# Revit family: Gira_277603
name_source: partatom
category: Electrical Fixtures
revit_build: Autodesk Revit 2017 (Build: 20160225_1515(x64)
units: mm (PartAtom-declared; Revit-internal decimal feet)

## family parameters
Cut with Voids When Loaded = No
Host = Face
Maintain Annotation Orientation = Yes
Part Type = Normal
Room Calculation Point = No
Round Connector Dimension = Use Diameter
Shared = No

## types (1)
- Sock.BS 13 A SH System 55 p.white
    Antibacterial treatment = No
    Available = No
    BIM (1) = https://media.stage.bim.site
    Category = Socket outlet
    Colour = White
    Connection type = Screwed terminal
    Cremeweiß glänzend = Cremeweiß glänzend
    Data sheet (1) = https://katalog.gira.de
    Default Elevation = 1219 mm
    Description = Sock.BS13A SH Sys55 PW,Socket outlet British Standard (BS 1363-2) 13 A 250 V~ with shutter,System 55, Support ring 71 x 71 mm,pure white glossy,Features:,- With screw terminals.,- For screw mounting only.
    Eject-mechanism = No
    Fault current protection = No
    Für "erschwerte Bedingungen" (nach VDE) (*de-DE) = No
    GTIN = 4010337079354
    HAN = 277603
    Halogen free = Yes
    HeinzeBIM = https://bimportal.heinze.de
    Imprint/indication = Without imprint
    Insulated mounting = No
    Label space/information surface = No
    Lockable = No
    Manufacturer = Gira
    Manufacturer URL = https://www.gira.de
    Material = Plastic
    Material quality = Thermoplastic
    Model = British Standard
    Mounting method = Flush mounted (plaster)
    Name = Sock.BS 13 A SH System 55 p.white
    Nominal current = 13
    Nominal voltage = 250
    Number of modules (module system) = 1
    Number of socket outlets switchable = 0
    Number of units = 1
    Over voltage protection = No
    Protective earth pin round = No
    RAL-number (akin) = 9010
    Rotated central insert = No
    Special power supply = No special power supply
    Suitable for degree of protection (IP) = IP20
    Surface finishing = Glossy
    Surface protection = Other
    Transparent = No
    Type of fastening = Mounting with screw
    URL = http://katalog.gira.de
    With built-in USB power supply = No
    With child-protection = Yes
    With function lighting = No
    With hinged lid = No
    With loop through function = No
    With miniature fuse = No
    With on/off switch = No
    With orientation lighting = No
    With signal lamp = No

## geometry (parser evidence)
native form markers: Sweep x1
no freeform markers — native parametric forms only
